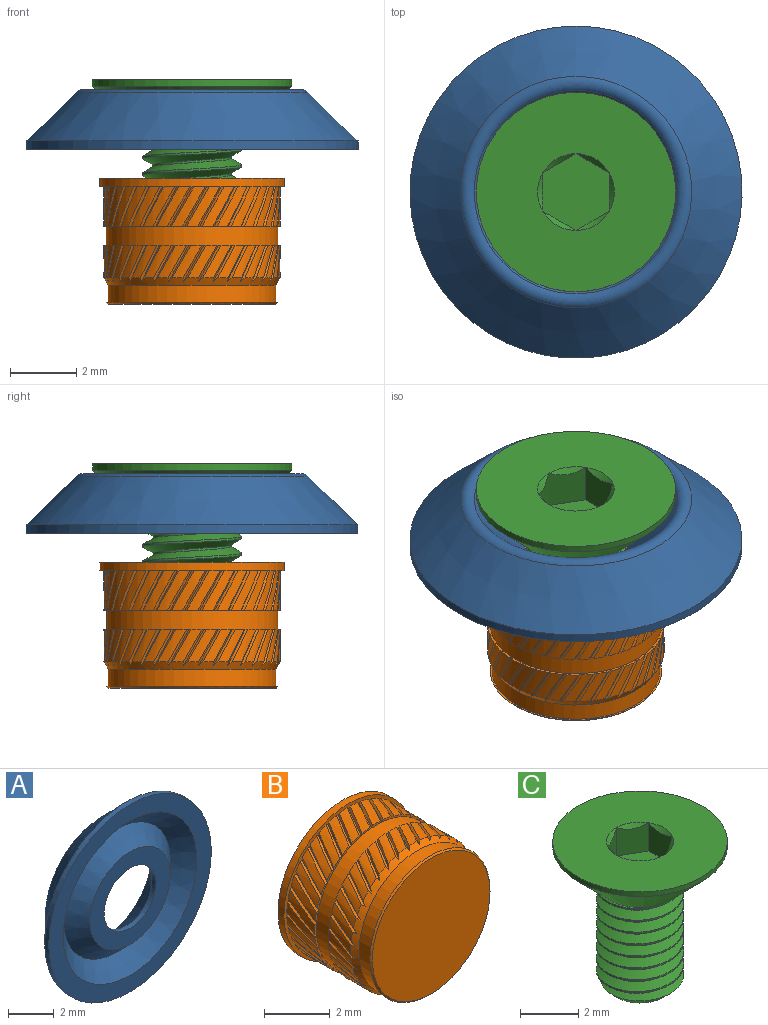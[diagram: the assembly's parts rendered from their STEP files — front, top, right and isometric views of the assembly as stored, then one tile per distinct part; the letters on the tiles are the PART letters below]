
ASSEMBLY  parts=3 mates=2
PART A: 9 faces, bbox 10x1.8x10 mm
  f0: cone r=2.16mm half-angle=45deg, axis (0,1,0), area 20.6mm2, adj f1,f8
  f1: cone r=2.93mm half-angle=46deg, axis (0,-1,0), area 27mm2, adj f0,f7
  f2: cone r=3.48mm half-angle=46deg, axis (0,-1,0), area 56.2mm2, adj f3,f6
  f3: cylinder r=5mm len=10mm, axis (0,-1,0), area 7.9mm2, adj f2,f7
  f4: cylinder r=1.6mm len=3.2mm, axis (0,-1,0), area 2.5mm2, adj f5,f8
  f5: cone r=1.6mm half-angle=45deg, axis (0,1,0), area 30.3mm2, adj f4,f6
  f6: torus R=3.27mm, axis (0,-1,0), area 9.6mm2, adj f2,f5
  f7: plane 10x10mm, normal (0,-1,0), area 25.3mm2, adj f1,f3
  f8: plane 4.95x4.95mm, normal (0,-1,0), area 11.2mm2, adj f0,f4
PART B: 227 faces, bbox 5.6x3.8x5.6 mm
  f0: cylinder r=2.58mm len=5.16mm, axis (0,1,0), area 9.3mm2, adj f225,f226
  f1: cone r=2.58mm half-angle=45deg, axis (0,1,0), area 1.2mm2, adj f151,f152
  f2: cone r=2.65mm half-angle=30deg, axis (0,1,0), area 3.9mm2, adj f5,f7,f8,f9,f10,f11,f12,f13
  f3: cylinder r=2.78mm len=5.56mm, axis (0,1,0), area 4.4mm2, adj f149,f150
  f4: cylinder r=2.65mm len=1.2mm, axis (0,1,0), area 0.4mm2, adj f149,f153,f156,f226
  f5: cylinder r=2.52mm len=5.05mm, axis (0,1,0), area 8.3mm2, adj f2,f151
  f6: cylinder r=2.65mm len=1.2mm, axis (0,1,0), area 0.4mm2, adj f149,f155,f158,f226
  f7: cylinder r=2.65mm len=0.97mm, axis (0,1,0), area 0.3mm2, adj f2,f47,f50,f225
  f8: cylinder r=2.65mm len=0.97mm, axis (0,1,0), area 0.3mm2, adj f2,f49,f51,f225
  f9: cylinder r=2.65mm len=0.97mm, axis (0,1,0), area 0.3mm2, adj f2,f111,f113,f225
  f10: cylinder r=2.65mm len=0.97mm, axis (0,1,0), area 0.3mm2, adj f2,f44,f114,f225
  f11: cylinder r=2.65mm len=0.97mm, axis (0,1,0), area 0.3mm2, adj f2,f109,f112,f225
  f12: cylinder r=2.65mm len=0.97mm, axis (0,1,0), area 0.3mm2, adj f2,f108,f110,f225
  f13: cylinder r=2.65mm len=0.97mm, axis (0,1,0), area 0.3mm2, adj f2,f103,f105,f225
  f14: cylinder r=2.65mm len=0.97mm, axis (0,1,0), area 0.3mm2, adj f2,f106,f107,f225
  f15: cylinder r=2.65mm len=0.97mm, axis (0,1,0), area 0.3mm2, adj f2,f101,f104,f225
  f16: cylinder r=2.65mm len=0.97mm, axis (0,1,0), area 0.3mm2, adj f2,f99,f102,f225
  f17: cylinder r=2.65mm len=0.97mm, axis (0,1,0), area 0.3mm2, adj f2,f97,f100,f225
  f18: cylinder r=2.65mm len=0.97mm, axis (0,1,0), area 0.3mm2, adj f2,f93,f95,f225
  f19: cylinder r=2.65mm len=0.97mm, axis (0,1,0), area 0.3mm2, adj f2,f96,f98,f225
  f20: cylinder r=2.65mm len=0.97mm, axis (0,1,0), area 0.3mm2, adj f2,f91,f94,f225
  f21: cylinder r=2.65mm len=0.97mm, axis (0,1,0), area 0.3mm2, adj f2,f90,f92,f225
  f22: cylinder r=2.65mm len=0.97mm, axis (0,1,0), area 0.3mm2, adj f2,f88,f89,f225
  f23: cylinder r=2.65mm len=0.97mm, axis (0,1,0), area 0.3mm2, adj f2,f85,f87,f225
  f24: cylinder r=2.65mm len=0.97mm, axis (0,1,0), area 0.3mm2, adj f2,f83,f86,f225
  f25: cylinder r=2.65mm len=0.97mm, axis (0,1,0), area 0.3mm2, adj f2,f81,f84,f225
  f26: cylinder r=2.65mm len=0.97mm, axis (0,1,0), area 0.3mm2, adj f2,f79,f82,f225
  f27: cylinder r=2.65mm len=0.97mm, axis (0,1,0), area 0.3mm2, adj f2,f78,f80,f225
  f28: cylinder r=2.65mm len=0.97mm, axis (0,1,0), area 0.3mm2, adj f2,f75,f77,f225
  f29: cylinder r=2.65mm len=0.97mm, axis (0,1,0), area 0.3mm2, adj f2,f73,f76,f225
  f30: cylinder r=2.65mm len=0.97mm, axis (0,1,0), area 0.3mm2, adj f2,f72,f74,f225
  f31: cylinder r=2.65mm len=0.97mm, axis (0,1,0), area 0.3mm2, adj f2,f67,f69,f225
  f32: cylinder r=2.65mm len=0.97mm, axis (0,1,0), area 0.3mm2, adj f2,f70,f71,f225
  f33: cylinder r=2.65mm len=0.97mm, axis (0,1,0), area 0.3mm2, adj f2,f65,f68,f225
  f34: cylinder r=2.65mm len=0.97mm, axis (0,1,0), area 0.3mm2, adj f2,f63,f66,f225
  f35: cylinder r=2.65mm len=0.97mm, axis (0,1,0), area 0.3mm2, adj f2,f61,f64,f225
  f36: cylinder r=2.65mm len=0.97mm, axis (0,1,0), area 0.3mm2, adj f2,f57,f59,f225
  f37: cylinder r=2.65mm len=0.97mm, axis (0,1,0), area 0.3mm2, adj f2,f60,f62,f225
  f38: cylinder r=2.65mm len=0.97mm, axis (0,1,0), area 0.3mm2, adj f2,f55,f58,f225
  f39: cylinder r=2.65mm len=0.97mm, axis (0,1,0), area 0.3mm2, adj f2,f52,f53,f225
  f40: cylinder r=2.65mm len=0.97mm, axis (0,1,0), area 0.3mm2, adj f2,f54,f56,f225
  f41: cylinder r=2.65mm len=0.97mm, axis (0,1,0), area 0.3mm2, adj f2,f45,f48,f225
  f42: cylinder r=2.65mm len=0.97mm, axis (0,1,0), area 0.3mm2, adj f2,f43,f46,f225
  f43: bspline ~1.08x0.57mm, area 0.1mm2, adj f2,f42,f44,f225
  f44: bspline ~1.21x0.69mm, area 0.1mm2, adj f2,f10,f43,f225
  f45: bspline ~1.08x0.63mm, area 0.1mm2, adj f2,f41,f46,f225
  f46: bspline ~1.21x0.74mm, area 0.1mm2, adj f2,f42,f45,f225
  f47: bspline ~1.08x0.67mm, area 0.1mm2, adj f2,f7,f48,f225
  f48: bspline ~1.21x0.76mm, area 0.1mm2, adj f2,f41,f47,f225
  f49: bspline ~1.08x0.69mm, area 0.1mm2, adj f2,f8,f50,f225
  f50: bspline ~1.21x0.76mm, area 0.1mm2, adj f2,f7,f49,f225
  f51: bspline ~1.31x0.79mm, area 0.1mm2, adj f2,f8,f52,f225
  f52: bspline ~1.31x0.81mm, area 0.1mm2, adj f2,f39,f51,f225
  f53: bspline ~1.31x0.74mm, area 0.1mm2, adj f2,f39,f54,f225
  f54: bspline ~1.31x0.78mm, area 0.1mm2, adj f2,f40,f53,f225
  f55: bspline ~1.21x0.67mm, area 0.1mm2, adj f2,f38,f56,f225
  f56: bspline ~1.21x0.62mm, area 0.1mm2, adj f2,f40,f55,f225
  f57: bspline ~1.21x0.6mm, area 0.1mm2, adj f2,f36,f58,f225
  f58: bspline ~1.21x0.54mm, area 0.1mm2, adj f2,f38,f57,f225
  f59: bspline ~1.31x0.67mm, area 0.1mm2, adj f2,f36,f60,f225
  f60: bspline ~1.31x0.6mm, area 0.1mm2, adj f2,f37,f59,f225
  f61: bspline ~1.08x0.57mm, area 0.1mm2, adj f2,f35,f62,f225
  f62: bspline ~1.21x0.69mm, area 0.1mm2, adj f2,f37,f61,f225
  f63: bspline ~1.08x0.63mm, area 0.1mm2, adj f2,f34,f64,f225
  f64: bspline ~1.21x0.74mm, area 0.1mm2, adj f2,f35,f63,f225
  f65: bspline ~1.08x0.67mm, area 0.1mm2, adj f2,f33,f66,f225
  f66: bspline ~1.21x0.76mm, area 0.1mm2, adj f2,f34,f65,f225
  f67: bspline ~1.08x0.69mm, area 0.1mm2, adj f2,f31,f68,f225
  f68: bspline ~1.21x0.76mm, area 0.1mm2, adj f2,f33,f67,f225
  f69: bspline ~1.31x0.79mm, area 0.1mm2, adj f2,f31,f70,f225
  f70: bspline ~1.31x0.81mm, area 0.1mm2, adj f2,f32,f69,f225
  f71: bspline ~1.31x0.74mm, area 0.1mm2, adj f2,f32,f72,f225
  f72: bspline ~1.31x0.78mm, area 0.1mm2, adj f2,f30,f71,f225
  f73: bspline ~1.21x0.67mm, area 0.1mm2, adj f2,f29,f74,f225
  f74: bspline ~1.21x0.62mm, area 0.1mm2, adj f2,f30,f73,f225
  f75: bspline ~1.21x0.6mm, area 0.1mm2, adj f2,f28,f76,f225
  f76: bspline ~1.21x0.54mm, area 0.1mm2, adj f2,f29,f75,f225
  f77: bspline ~1.31x0.67mm, area 0.1mm2, adj f2,f28,f78,f225
  f78: bspline ~1.31x0.6mm, area 0.1mm2, adj f2,f27,f77,f225
  f79: bspline ~1.08x0.57mm, area 0.1mm2, adj f2,f26,f80,f225
  f80: bspline ~1.21x0.69mm, area 0.1mm2, adj f2,f27,f79,f225
  f81: bspline ~1.08x0.63mm, area 0.1mm2, adj f2,f25,f82,f225
  f82: bspline ~1.21x0.74mm, area 0.1mm2, adj f2,f26,f81,f225
  f83: bspline ~1.08x0.67mm, area 0.1mm2, adj f2,f24,f84,f225
  f84: bspline ~1.21x0.76mm, area 0.1mm2, adj f2,f25,f83,f225
  f85: bspline ~1.08x0.69mm, area 0.1mm2, adj f2,f23,f86,f225
  f86: bspline ~1.21x0.76mm, area 0.1mm2, adj f2,f24,f85,f225
  f87: bspline ~1.31x0.79mm, area 0.1mm2, adj f2,f23,f88,f225
  f88: bspline ~1.31x0.81mm, area 0.1mm2, adj f2,f22,f87,f225
  f89: bspline ~1.31x0.74mm, area 0.1mm2, adj f2,f22,f90,f225
  f90: bspline ~1.31x0.78mm, area 0.1mm2, adj f2,f21,f89,f225
  f91: bspline ~1.21x0.67mm, area 0.1mm2, adj f2,f20,f92,f225
  f92: bspline ~1.21x0.62mm, area 0.1mm2, adj f2,f21,f91,f225
  f93: bspline ~1.21x0.6mm, area 0.1mm2, adj f2,f18,f94,f225
  f94: bspline ~1.21x0.54mm, area 0.1mm2, adj f2,f20,f93,f225
  f95: bspline ~1.31x0.67mm, area 0.1mm2, adj f2,f18,f96,f225
  f96: bspline ~1.31x0.6mm, area 0.1mm2, adj f2,f19,f95,f225
  f97: bspline ~1.08x0.57mm, area 0.1mm2, adj f2,f17,f98,f225
  f98: bspline ~1.21x0.69mm, area 0.1mm2, adj f2,f19,f97,f225
  f99: bspline ~1.08x0.63mm, area 0.1mm2, adj f2,f16,f100,f225
  f100: bspline ~1.21x0.74mm, area 0.1mm2, adj f2,f17,f99,f225
  f101: bspline ~1.08x0.67mm, area 0.1mm2, adj f2,f15,f102,f225
  f102: bspline ~1.21x0.76mm, area 0.1mm2, adj f2,f16,f101,f225
  f103: bspline ~1.08x0.69mm, area 0.1mm2, adj f2,f13,f104,f225
  f104: bspline ~1.21x0.76mm, area 0.1mm2, adj f2,f15,f103,f225
  f105: bspline ~1.31x0.79mm, area 0.1mm2, adj f2,f13,f106,f225
  f106: bspline ~1.31x0.81mm, area 0.1mm2, adj f2,f14,f105,f225
  f107: bspline ~1.31x0.74mm, area 0.1mm2, adj f2,f14,f108,f225
  f108: bspline ~1.31x0.78mm, area 0.1mm2, adj f2,f12,f107,f225
  f109: bspline ~1.21x0.67mm, area 0.1mm2, adj f2,f11,f110,f225
  f110: bspline ~1.21x0.62mm, area 0.1mm2, adj f2,f12,f109,f225
  f111: bspline ~1.21x0.6mm, area 0.1mm2, adj f2,f9,f112,f225
  f112: bspline ~1.21x0.54mm, area 0.1mm2, adj f2,f11,f111,f225
  f113: bspline ~1.31x0.67mm, area 0.1mm2, adj f2,f9,f114,f225
  f114: bspline ~1.31x0.6mm, area 0.1mm2, adj f2,f10,f113,f225
  f115: cylinder r=2.65mm len=1.2mm, axis (0,1,0), area 0.4mm2, adj f149,f221,f224,f226
  f116: cylinder r=2.65mm len=1.2mm, axis (0,1,0), area 0.4mm2, adj f149,f154,f223,f226
  f117: cylinder r=2.65mm len=1.2mm, axis (0,1,0), area 0.4mm2, adj f149,f219,f222,f226
  f118: cylinder r=2.65mm len=1.2mm, axis (0,1,0), area 0.4mm2, adj f149,f217,f220,f226
  f119: cylinder r=2.65mm len=1.2mm, axis (0,1,0), area 0.4mm2, adj f149,f213,f216,f226
  f120: cylinder r=2.65mm len=1.2mm, axis (0,1,0), area 0.4mm2, adj f149,f215,f218,f226
  f121: cylinder r=2.65mm len=1.2mm, axis (0,1,0), area 0.4mm2, adj f149,f211,f214,f226
  f122: cylinder r=2.65mm len=1.2mm, axis (0,1,0), area 0.4mm2, adj f149,f209,f212,f226
  f123: cylinder r=2.65mm len=1.2mm, axis (0,1,0), area 0.4mm2, adj f149,f207,f210,f226
  f124: cylinder r=2.65mm len=1.2mm, axis (0,1,0), area 0.4mm2, adj f149,f203,f206,f226
  f125: cylinder r=2.65mm len=1.2mm, axis (0,1,0), area 0.4mm2, adj f149,f205,f208,f226
  f126: cylinder r=2.65mm len=1.2mm, axis (0,1,0), area 0.4mm2, adj f149,f201,f204,f226
  f127: cylinder r=2.65mm len=1.2mm, axis (0,1,0), area 0.4mm2, adj f149,f199,f202,f226
  f128: cylinder r=2.65mm len=1.2mm, axis (0,1,0), area 0.4mm2, adj f149,f197,f200,f226
  f129: cylinder r=2.65mm len=1.2mm, axis (0,1,0), area 0.4mm2, adj f149,f195,f198,f226
  f130: cylinder r=2.65mm len=1.2mm, axis (0,1,0), area 0.4mm2, adj f149,f193,f196,f226
  f131: cylinder r=2.65mm len=1.2mm, axis (0,1,0), area 0.4mm2, adj f149,f191,f194,f226
  f132: cylinder r=2.65mm len=1.2mm, axis (0,1,0), area 0.4mm2, adj f149,f189,f192,f226
  f133: cylinder r=2.65mm len=1.2mm, axis (0,1,0), area 0.4mm2, adj f149,f187,f190,f226
  f134: cylinder r=2.65mm len=1.2mm, axis (0,1,0), area 0.4mm2, adj f149,f185,f188,f226
  f135: cylinder r=2.65mm len=1.2mm, axis (0,1,0), area 0.4mm2, adj f149,f183,f186,f226
  f136: cylinder r=2.65mm len=1.2mm, axis (0,1,0), area 0.4mm2, adj f149,f181,f184,f226
  f137: cylinder r=2.65mm len=1.2mm, axis (0,1,0), area 0.4mm2, adj f149,f177,f180,f226
  f138: cylinder r=2.65mm len=1.2mm, axis (0,1,0), area 0.4mm2, adj f149,f179,f182,f226
  f139: cylinder r=2.65mm len=1.2mm, axis (0,1,0), area 0.4mm2, adj f149,f175,f178,f226
  f140: cylinder r=2.65mm len=1.2mm, axis (0,1,0), area 0.4mm2, adj f149,f173,f176,f226
  f141: cylinder r=2.65mm len=1.2mm, axis (0,1,0), area 0.4mm2, adj f149,f171,f174,f226
  f142: cylinder r=2.65mm len=1.2mm, axis (0,1,0), area 0.4mm2, adj f149,f167,f170,f226
  f143: cylinder r=2.65mm len=1.2mm, axis (0,1,0), area 0.4mm2, adj f149,f169,f172,f226
  f144: cylinder r=2.65mm len=1.2mm, axis (0,1,0), area 0.4mm2, adj f149,f165,f168,f226
  f145: cylinder r=2.65mm len=1.2mm, axis (0,1,0), area 0.4mm2, adj f149,f161,f164,f226
  f146: cylinder r=2.65mm len=1.2mm, axis (0,1,0), area 0.4mm2, adj f149,f163,f166,f226
  f147: cylinder r=2.65mm len=1.2mm, axis (0,1,0), area 0.4mm2, adj f149,f159,f162,f226
  f148: cylinder r=2.65mm len=1.2mm, axis (0,1,0), area 0.4mm2, adj f149,f157,f160,f226
  f149: plane 5.56x5.56mm, normal (0,-1,0), area 2.3mm2, adj f3,f4,f6,f115,f116,f117,f118,f119
  f150: plane 5.56x5.56mm, normal (0,1,0), area 24.3mm2, adj f3
  f151: plane 5.16x5.16mm, normal (0,1,0), area 0.9mm2, adj f1,f5
  f152: plane 5.05x5.05mm, normal (0,-1,0), area 20mm2, adj f1
  f153: bspline ~1.31x0.79mm, area 0.1mm2, adj f4,f149,f154,f226
  f154: bspline ~1.31x0.81mm, area 0.1mm2, adj f116,f149,f153,f226
  f155: bspline ~1.31x0.81mm, area 0.1mm2, adj f6,f149,f156,f226
  f156: bspline ~1.31x0.81mm, area 0.1mm2, adj f4,f149,f155,f226
  f157: bspline ~1.31x0.81mm, area 0.1mm2, adj f148,f149,f158,f226
  f158: bspline ~1.31x0.78mm, area 0.1mm2, adj f6,f149,f157,f226
  f159: bspline ~1.2x0.71mm, area 0.1mm2, adj f147,f149,f160,f226
  f160: bspline ~1.31x0.73mm, area 0.1mm2, adj f148,f149,f159,f226
  f161: bspline ~1.31x0.72mm, area 0.1mm2, adj f145,f149,f162,f226
  f162: bspline ~1.31x0.66mm, area 0.1mm2, adj f147,f149,f161,f226
  f163: bspline ~1.31x0.64mm, area 0.1mm2, adj f146,f149,f164,f226
  f164: bspline ~1.31x0.58mm, area 0.1mm2, adj f145,f149,f163,f226
  f165: bspline ~1.2x0.56mm, area 0.1mm2, adj f144,f149,f166,f226
  f166: bspline ~1.31x0.67mm, area 0.1mm2, adj f146,f149,f165,f226
  f167: bspline ~1.2x0.64mm, area 0.1mm2, adj f142,f149,f168,f226
  f168: bspline ~1.31x0.74mm, area 0.1mm2, adj f144,f149,f167,f226
  f169: bspline ~1.31x0.75mm, area 0.1mm2, adj f143,f149,f170,f226
  f170: bspline ~1.31x0.79mm, area 0.1mm2, adj f142,f149,f169,f226
  f171: bspline ~1.31x0.79mm, area 0.1mm2, adj f141,f149,f172,f226
  f172: bspline ~1.31x0.81mm, area 0.1mm2, adj f143,f149,f171,f226
  f173: bspline ~1.31x0.81mm, area 0.1mm2, adj f140,f149,f174,f226
  f174: bspline ~1.31x0.81mm, area 0.1mm2, adj f141,f149,f173,f226
  f175: bspline ~1.31x0.81mm, area 0.1mm2, adj f139,f149,f176,f226
  f176: bspline ~1.31x0.78mm, area 0.1mm2, adj f140,f149,f175,f226
  f177: bspline ~1.2x0.71mm, area 0.1mm2, adj f137,f149,f178,f226
  f178: bspline ~1.31x0.73mm, area 0.1mm2, adj f139,f149,f177,f226
  f179: bspline ~1.31x0.72mm, area 0.1mm2, adj f138,f149,f180,f226
  f180: bspline ~1.31x0.66mm, area 0.1mm2, adj f137,f149,f179,f226
  f181: bspline ~1.31x0.64mm, area 0.1mm2, adj f136,f149,f182,f226
  f182: bspline ~1.31x0.58mm, area 0.1mm2, adj f138,f149,f181,f226
  f183: bspline ~1.2x0.56mm, area 0.1mm2, adj f135,f149,f184,f226
  f184: bspline ~1.31x0.67mm, area 0.1mm2, adj f136,f149,f183,f226
  f185: bspline ~1.2x0.64mm, area 0.1mm2, adj f134,f149,f186,f226
  f186: bspline ~1.31x0.74mm, area 0.1mm2, adj f135,f149,f185,f226
  f187: bspline ~1.31x0.75mm, area 0.1mm2, adj f133,f149,f188,f226
  f188: bspline ~1.31x0.79mm, area 0.1mm2, adj f134,f149,f187,f226
  f189: bspline ~1.31x0.79mm, area 0.1mm2, adj f132,f149,f190,f226
  f190: bspline ~1.31x0.81mm, area 0.1mm2, adj f133,f149,f189,f226
  f191: bspline ~1.31x0.81mm, area 0.1mm2, adj f131,f149,f192,f226
  f192: bspline ~1.31x0.81mm, area 0.1mm2, adj f132,f149,f191,f226
  f193: bspline ~1.31x0.81mm, area 0.1mm2, adj f130,f149,f194,f226
  f194: bspline ~1.31x0.78mm, area 0.1mm2, adj f131,f149,f193,f226
  f195: bspline ~1.2x0.71mm, area 0.1mm2, adj f129,f149,f196,f226
  f196: bspline ~1.31x0.73mm, area 0.1mm2, adj f130,f149,f195,f226
  f197: bspline ~1.31x0.72mm, area 0.1mm2, adj f128,f149,f198,f226
  f198: bspline ~1.31x0.66mm, area 0.1mm2, adj f129,f149,f197,f226
  f199: bspline ~1.31x0.64mm, area 0.1mm2, adj f127,f149,f200,f226
  f200: bspline ~1.31x0.58mm, area 0.1mm2, adj f128,f149,f199,f226
  f201: bspline ~1.2x0.56mm, area 0.1mm2, adj f126,f149,f202,f226
  f202: bspline ~1.31x0.67mm, area 0.1mm2, adj f127,f149,f201,f226
  f203: bspline ~1.2x0.64mm, area 0.1mm2, adj f124,f149,f204,f226
  f204: bspline ~1.31x0.74mm, area 0.1mm2, adj f126,f149,f203,f226
  f205: bspline ~1.31x0.75mm, area 0.1mm2, adj f125,f149,f206,f226
  f206: bspline ~1.31x0.79mm, area 0.1mm2, adj f124,f149,f205,f226
  f207: bspline ~1.31x0.79mm, area 0.1mm2, adj f123,f149,f208,f226
  f208: bspline ~1.31x0.81mm, area 0.1mm2, adj f125,f149,f207,f226
  f209: bspline ~1.31x0.81mm, area 0.1mm2, adj f122,f149,f210,f226
  f210: bspline ~1.31x0.81mm, area 0.1mm2, adj f123,f149,f209,f226
  f211: bspline ~1.31x0.81mm, area 0.1mm2, adj f121,f149,f212,f226
  f212: bspline ~1.31x0.78mm, area 0.1mm2, adj f122,f149,f211,f226
  f213: bspline ~1.2x0.71mm, area 0.1mm2, adj f119,f149,f214,f226
  f214: bspline ~1.31x0.73mm, area 0.1mm2, adj f121,f149,f213,f226
  f215: bspline ~1.31x0.72mm, area 0.1mm2, adj f120,f149,f216,f226
  f216: bspline ~1.31x0.66mm, area 0.1mm2, adj f119,f149,f215,f226
  f217: bspline ~1.31x0.64mm, area 0.1mm2, adj f118,f149,f218,f226
  f218: bspline ~1.31x0.58mm, area 0.1mm2, adj f120,f149,f217,f226
  f219: bspline ~1.2x0.56mm, area 0.1mm2, adj f117,f149,f220,f226
  f220: bspline ~1.31x0.67mm, area 0.1mm2, adj f118,f149,f219,f226
  f221: bspline ~1.2x0.64mm, area 0.1mm2, adj f115,f149,f222,f226
  f222: bspline ~1.31x0.74mm, area 0.1mm2, adj f117,f149,f221,f226
  f223: bspline ~1.31x0.75mm, area 0.1mm2, adj f116,f149,f224,f226
  f224: bspline ~1.31x0.79mm, area 0.1mm2, adj f115,f149,f223,f226
  f225: plane 5.31x5.31mm, normal (0,1,0), area 1.1mm2, adj f0,f7,f8,f9,f10,f11,f12,f13
  f226: plane 5.31x5.31mm, normal (0,-1,0), area 1.1mm2, adj f0,f4,f6,f115,f116,f117,f118,f119
PART C: 23 faces, bbox 6.4x6.4x6.6 mm
  f0: cone r=1.15mm half-angle=45deg, axis (0,0,1), area 0.1mm2, adj f10,f17
  f1: cone r=1.5mm half-angle=45deg, axis (0,0,1), area 31.8mm2, adj f2,f3,f6,f7,f8
  f2: cone r=1.5mm half-angle=45deg, axis (0,0,1), area 0.2mm2, adj f1,f5,f7,f8
  f3: cylinder r=3mm len=6mm, axis (0,0,1), area 3.8mm2, adj f1,f10
  f4: cone r=1.12mm half-angle=45deg, axis (0,0,1), area 2.4mm2, adj f5,f6,f7,f8,f9
  f5: cylinder r=1.18mm len=3.93mm, axis (0,0,1), area 3.6mm2, adj f2,f4,f7,f8
  f6: cylinder r=1.5mm len=3.93mm, axis (0,0,-1), area 4.6mm2, adj f1,f4,f7,f8
  f7: bspline ~4.69x3.46mm, area 24.8mm2, adj f1,f2,f4,f5,f6
  f8: bspline ~4.35x3.46mm, area 24.8mm2, adj f1,f2,f4,f5,f6
  f9: plane 2.25x2.25mm, normal (0,0,-1), area 4mm2, adj f4
  f10: plane 6x6mm, normal (0,0,1), area 24.1mm2, adj f0,f3,f11,f12,f13,f14,f15
  f11: cone r=1.15mm half-angle=45deg, axis (0,0,1), area 0mm2, adj f10,f18
  f12: cone r=1.15mm half-angle=45deg, axis (0,0,1), area 0mm2, adj f10,f19
  f13: cone r=1.15mm half-angle=45deg, axis (0,0,1), area 0mm2, adj f10,f20
  f14: cone r=1.15mm half-angle=45deg, axis (0,0,1), area 0mm2, adj f10,f21
  f15: cone r=1.15mm half-angle=45deg, axis (0,0,1), area 0mm2, adj f10,f22
  f16: plane 2.31x2mm, normal (0,0,1), area 3.5mm2, adj f17,f18,f19,f20,f21,f22
  f17: plane 1.3x1.27mm, normal (-1,0,0), area 1.3mm2, adj f0,f16,f18,f22
  f18: plane 1.63x1.44mm, normal (-0.5,-0.87,0), area 1.3mm2, adj f11,f16,f17,f19
  f19: plane 1.63x1.44mm, normal (0.5,-0.87,0), area 1.3mm2, adj f12,f16,f18,f20
  f20: plane 1.63x1.59mm, normal (1,0,0), area 1.3mm2, adj f13,f16,f19,f21
  f21: plane 1.63x1.44mm, normal (0.5,0.87,0), area 1.3mm2, adj f14,f16,f20,f22
  f22: plane 1.63x1.44mm, normal (-0.5,0.87,0), area 1.3mm2, adj f15,f16,f17,f21
PLACE A rot(axis=(1,0,0),90deg) t=(0,0,-2.1)mm
PLACE B rot(axis=(1,0,0),90deg) t=(0,0,-2.96)mm
PLACE C at identity fixed
MATE fastened A.f0 <-> C.f3  axis (0,0,-1) through (0,0,-1.11)mm
MATE fastened B.f2 <-> C.f3  axis (0,0,-1) through (0,0,-6.76)mm
